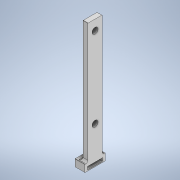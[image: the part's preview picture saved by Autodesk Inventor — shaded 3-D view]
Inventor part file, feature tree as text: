
AUTODESK INVENTOR PART (.ipt)
format: ipt  version: 2021.4 (Build 254397000, 397)  size: 167,424 bytes
history: native  units: mm
features: sketch x5, extrude x4, fillet x2, other x1, hole x1
ambient origin geometry x8: Origin, YZ Plane, XZ Plane, XY Plane, X Axis, Y Axis, Z Axis, Center Point
bodies: Body1 (feature_tree)
feature tree (13):
  other  "ソリッド1"
  extrude  "押し出し1"  Depth=10.0mm
  extrude  "押し出し2"  Depth=20.0mm
  extrude  "押し出し3"  Depth=6.0mm TaperAngle=0.0deg
  extrude  "押し出し4"  Depth=15.0mm
  fillet  "フィレット1"  Radius=3.0mm
  fillet  "フィレット2"  Radius=10.0mm
  hole  "穴1"  [1 undecoded]
  sketch  "スケッチ1"
  sketch  "スケッチ2"
  sketch  "スケッチ3"
  sketch  "スケッチ4"
  sketch  "スケッチ5"
note: 1 required parameter value undecoded (feature->parameter linkage not recoverable at this tier; creation-order binding heuristic only, values carry confidence <= 0.55)
